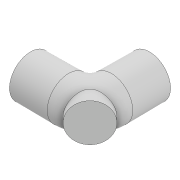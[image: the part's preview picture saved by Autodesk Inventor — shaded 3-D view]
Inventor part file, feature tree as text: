
AUTODESK INVENTOR PART (.ipt)
format: ipt  version: 2020 (Build 240168000, 168)  size: 183,808 bytes
history: native  units: mm
features: sketch x4, revolve x3, plane x2, extrude x1, projected_geometry x1
ambient origin geometry x8: Origin, YZ Plane, XZ Plane, XY Plane, X Axis, Y Axis, Z Axis, Center Point
bodies: Solid1 (feature_tree)
feature tree (11):
  revolve  "Revolution1"  [1 undecoded]
  revolve  "Revolution2"  [1 undecoded]
  revolve  "Revolution3"  [1 undecoded]
  plane  "Work Plane2"
  extrude  "Extrusion1"  Depth=10.0mm
  sketch  "Sketch1"  dims[d0=11.0mm d1=20.0mm]
  sketch  "Sketch2"  dims[d2=11.2mm d3=1.6mm]
  sketch  "Sketch3"  dims[d4=90.0deg d5=11.2mm]
  plane  "Work Plane1"
  sketch  "Sketch4"  dims[d6=90.0deg d7=20.0mm d8=90.0deg d9=11.0mm d10=1.6mm d11=90.0deg d12=-7.853982mm d13=30.0mm d14=20.0mm d15=10.0mm d16=0.0mm]
  projected_geometry  "Projected Loop1"
note: 3 required parameter values undecoded (feature->parameter linkage not recoverable at this tier; creation-order binding heuristic only, values carry confidence <= 0.55)
